# Revit family: 3-28-xxxx - Bonzo Chandelier
name_source: partatom
category: Lighting Fixtures
revit_build: Autodesk Revit 2018 (Build: 20170223_1515(x64)
units: mm (PartAtom-declared; Revit-internal decimal feet)

## family parameters
Always vertical = Yes
Cut with Voids When Loaded = No
Host = Ceiling
Light Source = Yes
OmniClass Number = 23.80.70.11
OmniClass Title = Luminaries for Internal Lighting
Part Type = Normal
Room Calculation Point = No
Round Connector Dimension = Use Diameter
Shared = No

## types (1)
- 3-28-1540 / Black - Aged Brass - Matte White Acrylic
    Color Filter = 16777215
    Diffusers = Matte White Acrylic
    Dimming Lamp Color Temperature Shift = <None>
    Lamp = LED Array
    Light Source Symbol Size = 610 mm
    Manufacturer = Oxygen Lighting and Fans
    Metal Finish 1 = 15 - Black
    Metal Finish 2 = 40 - Aged Brass
    Model = 3-28-xxxx / Bonzo Chandelier
    References = Ref. 3 = 120 V / Ref. 37 = 277 V
    URL = www.oxygenlighting.com
    Voltage = 120 V
    Voltage Input = 120 V or 277 V - 50/60 Hz
    Wattage Comments = 8 x 3.9W at 120

## geometry (parser evidence)
native form markers: Sweep x7
no freeform markers — native parametric forms only
